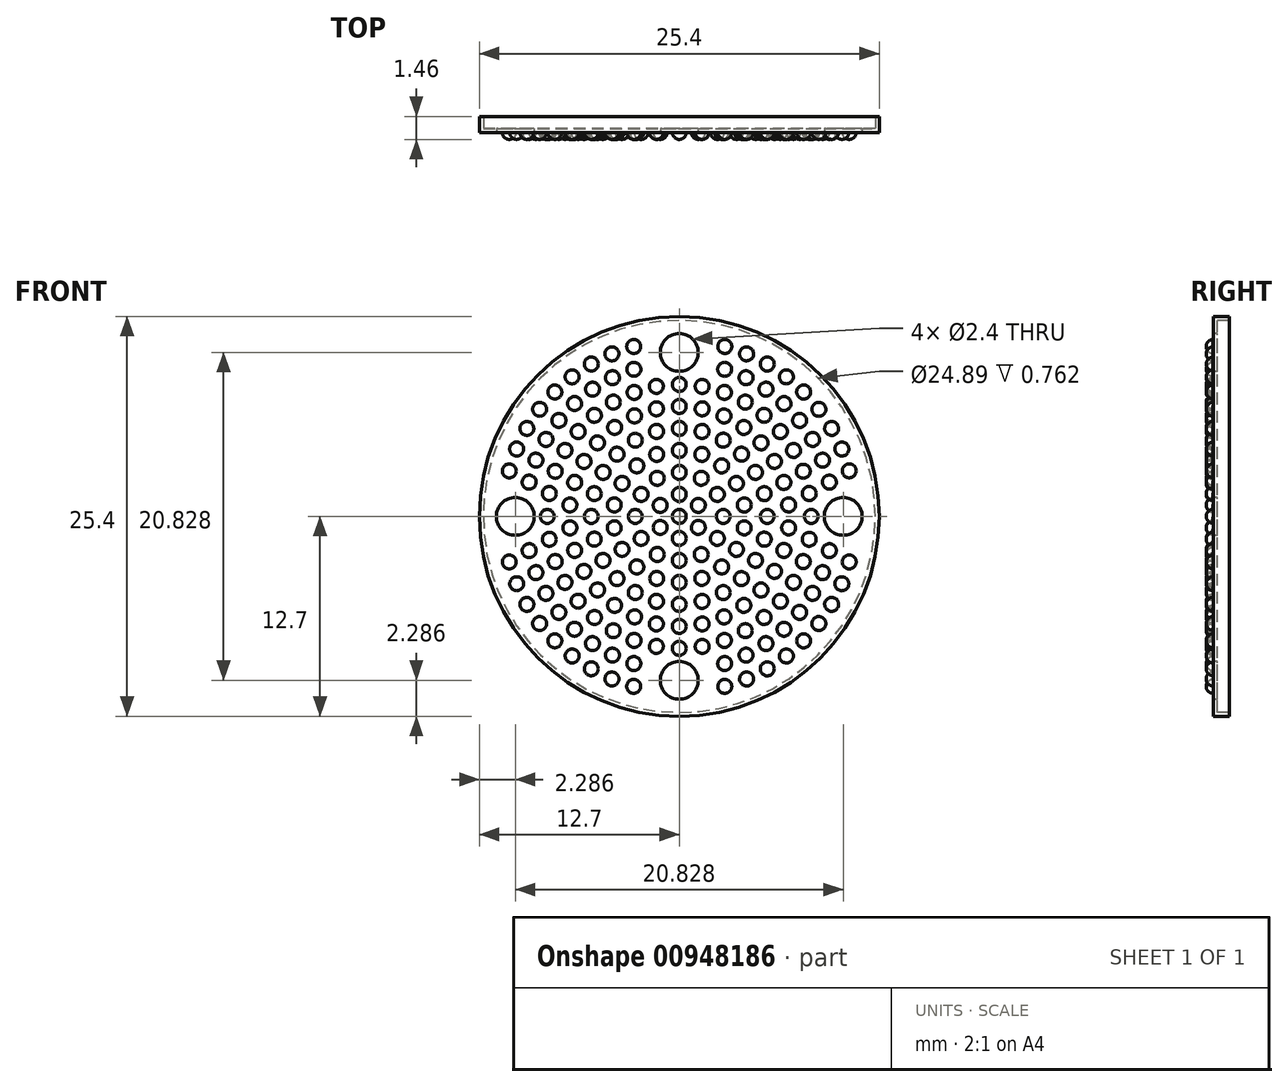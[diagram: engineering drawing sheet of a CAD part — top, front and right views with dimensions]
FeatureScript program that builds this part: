
annotation { "Feature Type Name" : "Feature", "Feature Type Description" : "" }
export const myFeature = defineFeature(function(context is Context, id is Id, definition is map)
    precondition{}
    {
        {
            var Q0;
            Q0=qCreatedBy(makeId("Front.planeOp"),FACE);
            var sketch = newSketch(context, id + "F0", { "sketchPlane" : qUnion([Q0])});
            skCircle(sketch, "E0", {"center": v(0, 0) * mm, "radius": 12.45 * mm});
            skCircle(sketch, "E1.0", {"center": v(0, 0) * mm, "radius": 12.7 * mm});
            skPoint(sketch, "E2", {"position": v(0, 10.41) * mm});
            skPoint(sketch, "E3.3.0", {"position": v(0, 11.18) * mm});
            skPoint(sketch, "E4.1.0", {"position": v(10.41, 0) * mm});
            skPoint(sketch, "E4.2.0", {"position": v(0, -10.41) * mm});
            skPoint(sketch, "E4.3.0", {"position": v(-10.41, 0) * mm});
            skLineSegment(sketch, "E4.anchor1", {"start": v(0, 0) * mm, "end": v(0, 10.41) * mm, "construction": true});
            skLineSegment(sketch, "E4.anchor2", {"start": v(0, 0) * mm, "end": v(-10.41, 0) * mm, "construction": true});
            skSolve(sketch);
        }
        {
            var Q0;
            Q0=makeQuery(id+"F0.imprint","IMPRINT",FACE,{"disambiguationData":[TD([[makeQuery(id+"F0.imprint","IMPRINT",EDGE,{"derivedFrom":sQuery(id+"F0.wireOp",EDGE,"E0")}),1.0]])]});
            extrude(context, id + "F1", {"entities" : qUnion([Q0]), "depth" : -0.25 * mm, "offsetDistance" : 25.4 * mm});
        }
        {
            var Q0;
            Q0=makeQuery(id+"F0.imprint","IMPRINT",FACE,{"disambiguationData":[TD([[makeQuery(id+"F0.imprint","IMPRINT",EDGE,{"derivedFrom":sQuery(id+"F0.wireOp",EDGE,"E0")}),-1.0]])]});
            extrude(context, id + "F2", {"entities" : qUnion([Q0]), "operationType" : NewBodyOperationType.ADD, "depth" : -1.02 * mm, "offsetDistance" : 25.4 * mm});
        }
        {
            var Q0;
            Q0=qCreatedBy(makeId("Right.planeOp"),FACE);
            var sketch = newSketch(context, id + "F3", { "sketchPlane" : qUnion([Q0])});
            skArc(sketch, "E5", {"start": v(0, 0.44) * mm, "mid": v(-0.44, 0) * mm, "end": v(0, -0.44) * mm});
            skLineSegment(sketch, "E6", {"start": v(0, 0.44) * mm, "end": v(0, -0.44) * mm});
            skArc(sketch, "E7.0.1.0", {"start": v(0, 1.84) * mm, "mid": v(-0.44, 1.4) * mm, "end": v(0, 0.95) * mm});
            skLineSegment(sketch, "E7.0.1.1", {"start": v(0, 1.84) * mm, "end": v(0, 0.95) * mm});
            skArc(sketch, "E7.0.2.0", {"start": v(0, 3.24) * mm, "mid": v(-0.44, 2.8) * mm, "end": v(0, 2.35) * mm});
            skLineSegment(sketch, "E7.0.2.1", {"start": v(0, 3.24) * mm, "end": v(0, 2.35) * mm});
            skArc(sketch, "E7.0.3.0", {"start": v(0, 4.64) * mm, "mid": v(-0.44, 4.2) * mm, "end": v(0, 3.75) * mm});
            skLineSegment(sketch, "E7.0.3.1", {"start": v(0, 4.64) * mm, "end": v(0, 3.75) * mm});
            skArc(sketch, "E7.0.4.0", {"start": v(0, 6.03) * mm, "mid": v(-0.44, 5.59) * mm, "end": v(0, 5.14) * mm});
            skLineSegment(sketch, "E7.0.4.1", {"start": v(0, 6.03) * mm, "end": v(0, 5.14) * mm});
            skArc(sketch, "E7.0.5.0", {"start": v(0, 7.43) * mm, "mid": v(-0.44, 6.99) * mm, "end": v(0, 6.54) * mm});
            skLineSegment(sketch, "E7.0.5.1", {"start": v(0, 7.43) * mm, "end": v(0, 6.54) * mm});
            skArc(sketch, "E7.0.6.0", {"start": v(0, 8.83) * mm, "mid": v(-0.44, 8.38) * mm, "end": v(0, 7.94) * mm});
            skLineSegment(sketch, "E7.0.6.1", {"start": v(0, 8.83) * mm, "end": v(0, 7.94) * mm});
            skArc(sketch, "E7.0.7.0", {"start": v(0, 10.22) * mm, "mid": v(-0.44, 9.78) * mm, "end": v(0, 9.33) * mm});
            skLineSegment(sketch, "E7.0.7.1", {"start": v(0, 10.22) * mm, "end": v(0, 9.33) * mm});
            skArc(sketch, "E7.0.8.0", {"start": v(0, 11.62) * mm, "mid": v(-0.44, 11.18) * mm, "end": v(0, 10.73) * mm});
            skLineSegment(sketch, "E7.0.8.1", {"start": v(0, 11.62) * mm, "end": v(0, 10.73) * mm});
            skLineSegment(sketch, "E7.direction1", {"start": v(0, -0.44) * mm, "end": v(25.4, -0.44) * mm, "construction": true});
            skLineSegment(sketch, "E7.direction2", {"start": v(0, -0.44) * mm, "end": v(0, 0.95) * mm, "construction": true});
            skLineSegment(sketch, "E8", {"start": v(0, 0) * mm, "end": v(-1.18, 0) * mm});
            skSolve(sketch);
        }
        {
            var Q0;
            Q0=makeQuery(id+"F3.imprint","IMPRINT",FACE,{"disambiguationData":[TD([[makeQuery(id+"F3.imprint","IMPRINT",EDGE,{"derivedFrom":sQuery(id+"F3.wireOp",EDGE,"E7.0.8.0")}),1.0]])]});
            var Q1;
            Q1=makeQuery(id+"F3.imprint","IMPRINT",FACE,{"disambiguationData":[TD([[makeQuery(id+"F3.imprint","IMPRINT",EDGE,{"derivedFrom":sQuery(id+"F3.wireOp",EDGE,"E7.0.7.0")}),1.0]])]});
            var Q2;
            Q2=makeQuery(id+"F3.imprint","IMPRINT",FACE,{"disambiguationData":[TD([[makeQuery(id+"F3.imprint","IMPRINT",EDGE,{"derivedFrom":sQuery(id+"F3.wireOp",EDGE,"E7.0.6.0")}),1.0]])]});
            var Q3;
            Q3=makeQuery(id+"F3.imprint","IMPRINT",FACE,{"disambiguationData":[TD([[makeQuery(id+"F3.imprint","IMPRINT",EDGE,{"derivedFrom":sQuery(id+"F3.wireOp",EDGE,"E7.0.5.0")}),1.0]])]});
            var Q4;
            Q4=makeQuery(id+"F3.imprint","IMPRINT",FACE,{"disambiguationData":[TD([[makeQuery(id+"F3.imprint","IMPRINT",EDGE,{"derivedFrom":sQuery(id+"F3.wireOp",EDGE,"E7.0.4.0")}),1.0]])]});
            var Q5;
            Q5=makeQuery(id+"F3.imprint","IMPRINT",FACE,{"disambiguationData":[TD([[makeQuery(id+"F3.imprint","IMPRINT",EDGE,{"derivedFrom":sQuery(id+"F3.wireOp",EDGE,"E7.0.3.0")}),1.0]])]});
            var Q6;
            Q6=makeQuery(id+"F3.imprint","IMPRINT",FACE,{"disambiguationData":[TD([[makeQuery(id+"F3.imprint","IMPRINT",EDGE,{"derivedFrom":sQuery(id+"F3.wireOp",EDGE,"E7.0.2.0")}),1.0]])]});
            var Q7;
            Q7=makeQuery(id+"F3.imprint","IMPRINT",FACE,{"disambiguationData":[TD([[makeQuery(id+"F3.imprint","IMPRINT",EDGE,{"derivedFrom":sQuery(id+"F3.wireOp",EDGE,"E7.0.1.0")}),1.0]])]});
            var Q8;
            Q8=sQuery(id+"F3.wireOp",EDGE,"E6");
            revolve(context, id + "F4", {"surfaceOperationType" : NewSurfaceOperationType.NEW, "entities" : qUnion([Q0, Q1, Q2, Q3, Q4, Q5, Q6, Q7]), "axis" : qUnion([Q8]), "revolveType" : RevolveType.TWO_DIRECTIONS, "angle" : 92 * degree, "angleBack" : 272 * degree});
        }
        {
            var Q0;
            {var subQ0=sQuery(id+"F3.wireOp",EDGE,"E6");var subQ1=sQuery(id+"F3.wireOp",EDGE,"E5");var subQ2=makeQuery(id+"F3.imprint","INTERSECT",VERTEX,{"disambiguationData":[OD(1.0)],"derivedFrom":[subQ1,subQ0]});Q0=makeQuery(id+"F3.imprint","IMPRINT",FACE,{"disambiguationData":[TD([[makeQuery(id+"F3.imprint","IMPRINT",EDGE,{"disambiguationData":[TD([[subQ2,1.0]])],"derivedFrom":subQ1}),1.0]])]});}
            var Q1;
            {var subQ0=sQuery(id+"F3.wireOp",EDGE,"E6");var subQ1=sQuery(id+"F3.wireOp",EDGE,"E5");var subQ2=makeQuery(id+"F3.imprint","INTERSECT",VERTEX,{"disambiguationData":[OD(0.0)],"derivedFrom":[subQ1,subQ0]});Q1=makeQuery(id+"F3.imprint","IMPRINT",FACE,{"disambiguationData":[TD([[makeQuery(id+"F3.imprint","IMPRINT",EDGE,{"disambiguationData":[TD([[subQ2,-1.0]])],"derivedFrom":subQ1}),1.0]])]});}
            var Q2;
            Q2=sQuery(id+"F3.wireOp",EDGE,"E6");
            revolve(context, id + "F5", {"operationType" : NewBodyOperationType.ADD, "surfaceOperationType" : NewSurfaceOperationType.NEW, "entities" : qUnion([Q0, Q1]), "axis" : qUnion([Q2]), "revolveType" : RevolveType.TWO_DIRECTIONS, "angle" : 92 * degree, "angleBack" : 272 * degree});
        }
        {
            var Q0;
            Q0=makeQuery(id+"F4.opRevolve","SWEPT_BODY",BODY,{"disambiguationData":[OSD([sQuery(id+"F3.wireOp",EDGE,"E7.0.1.0"),sQuery(id+"F3.wireOp",EDGE,"E7.0.1.1")])]});
            var Q1;
            Q1=sQuery(id+"F3.wireOp",EDGE,"E8");
            circularPattern(context, id + "F6", {"entities" : qUnion([Q0]), "axis" : qUnion([Q1]), "angle" : 360 * degree, "instanceCount" : 6, "equalSpace" : true});
        }
        {
            var Q0;
            Q0=makeQuery(id+"F4.opRevolve","SWEPT_BODY",BODY,{"disambiguationData":[OSD([sQuery(id+"F3.wireOp",EDGE,"E7.0.2.0"),sQuery(id+"F3.wireOp",EDGE,"E7.0.2.1")])]});
            var Q1;
            Q1=sQuery(id+"F3.wireOp",EDGE,"E8");
            circularPattern(context, id + "F7", {"entities" : qUnion([Q0]), "axis" : qUnion([Q1]), "angle" : 360 * degree, "instanceCount" : 12, "equalSpace" : true});
        }
        {
            var Q0;
            Q0=makeQuery(id+"F4.opRevolve","SWEPT_BODY",BODY,{"disambiguationData":[OSD([sQuery(id+"F3.wireOp",EDGE,"E7.0.3.0"),sQuery(id+"F3.wireOp",EDGE,"E7.0.3.1")])]});
            var Q1;
            Q1=sQuery(id+"F3.wireOp",EDGE,"E8");
            circularPattern(context, id + "F8", {"entities" : qUnion([Q0]), "axis" : qUnion([Q1]), "angle" : 360 * degree, "instanceCount" : 18, "equalSpace" : true});
        }
        {
            var Q0;
            Q0=makeQuery(id+"F4.opRevolve","SWEPT_BODY",BODY,{"disambiguationData":[OSD([sQuery(id+"F3.wireOp",EDGE,"E7.0.4.0"),sQuery(id+"F3.wireOp",EDGE,"E7.0.4.1")])]});
            var Q1;
            Q1=sQuery(id+"F3.wireOp",EDGE,"E8");
            circularPattern(context, id + "F9", {"entities" : qUnion([Q0]), "axis" : qUnion([Q1]), "angle" : 360 * degree, "instanceCount" : 24, "equalSpace" : true});
        }
        {
            var Q0;
            Q0=makeQuery(id+"F4.opRevolve","SWEPT_BODY",BODY,{"disambiguationData":[OSD([sQuery(id+"F3.wireOp",EDGE,"E7.0.5.0"),sQuery(id+"F3.wireOp",EDGE,"E7.0.5.1")])]});
            var Q1;
            Q1=sQuery(id+"F3.wireOp",EDGE,"E8");
            circularPattern(context, id + "F10", {"entities" : qUnion([Q0]), "axis" : qUnion([Q1]), "angle" : 360 * degree, "instanceCount" : 30, "equalSpace" : true});
        }
        {
            var Q0;
            Q0=makeQuery(id+"F4.opRevolve","SWEPT_BODY",BODY,{"disambiguationData":[OSD([sQuery(id+"F3.wireOp",EDGE,"E7.0.6.0"),sQuery(id+"F3.wireOp",EDGE,"E7.0.6.1")])]});
            var Q1;
            Q1=sQuery(id+"F3.wireOp",EDGE,"E8");
            circularPattern(context, id + "F11", {"entities" : qUnion([Q0]), "axis" : qUnion([Q1]), "angle" : 360 * degree, "instanceCount" : 36, "equalSpace" : true});
        }
        {
            var Q0;
            Q0=makeQuery(id+"F4.opRevolve","SWEPT_BODY",BODY,{"disambiguationData":[OSD([sQuery(id+"F3.wireOp",EDGE,"E7.0.7.0"),sQuery(id+"F3.wireOp",EDGE,"E7.0.7.1")])]});
            var Q1;
            Q1=sQuery(id+"F3.wireOp",EDGE,"E8");
            circularPattern(context, id + "F12", {"entities" : qUnion([Q0]), "axis" : qUnion([Q1]), "angle" : 360 * degree, "instanceCount" : 42, "equalSpace" : true});
        }
        {
            var Q0;
            Q0=makeQuery(id+"F4.opRevolve","SWEPT_BODY",BODY,{"disambiguationData":[OSD([sQuery(id+"F3.wireOp",EDGE,"E7.0.8.0"),sQuery(id+"F3.wireOp",EDGE,"E7.0.8.1")])]});
            var Q1;
            Q1=sQuery(id+"F3.wireOp",EDGE,"E8");
            circularPattern(context, id + "F13", {"entities" : qUnion([Q0]), "axis" : qUnion([Q1]), "angle" : 360 * degree, "instanceCount" : 48, "equalSpace" : true});
        }
        {
            var Q0;
            Q0=makeQuery(id+"F13.opPattern","COPY",BODY,{"derivedFrom":makeQuery(id+"F4.opRevolve","SWEPT_BODY",BODY,{"disambiguationData":[OSD([sQuery(id+"F3.wireOp",EDGE,"E7.0.8.0"),sQuery(id+"F3.wireOp",EDGE,"E7.0.8.1")])]}),"instanceName":"24"});
            deleteBodies(context, id + "F14", {"entities" : qUnion([Q0])});
        }
        {
            var Q0;
            Q0=makeQuery(id+"F13.opPattern","COPY",BODY,{"derivedFrom":makeQuery(id+"F4.opRevolve","SWEPT_BODY",BODY,{"disambiguationData":[OSD([sQuery(id+"F3.wireOp",EDGE,"E7.0.8.0"),sQuery(id+"F3.wireOp",EDGE,"E7.0.8.1")])]}),"instanceName":"36"});
            var Q1;
            Q1=makeQuery(id+"F4.opRevolve","SWEPT_BODY",BODY,{"disambiguationData":[OSD([sQuery(id+"F3.wireOp",EDGE,"E7.0.8.0"),sQuery(id+"F3.wireOp",EDGE,"E7.0.8.1")])]});
            var Q2;
            Q2=makeQuery(id+"F13.opPattern","COPY",BODY,{"derivedFrom":makeQuery(id+"F4.opRevolve","SWEPT_BODY",BODY,{"disambiguationData":[OSD([sQuery(id+"F3.wireOp",EDGE,"E7.0.8.0"),sQuery(id+"F3.wireOp",EDGE,"E7.0.8.1")])]}),"instanceName":"12"});
            var Q3;
            Q3=makeQuery(id+"F13.opPattern","COPY",BODY,{"derivedFrom":makeQuery(id+"F4.opRevolve","SWEPT_BODY",BODY,{"disambiguationData":[OSD([sQuery(id+"F3.wireOp",EDGE,"E7.0.8.0"),sQuery(id+"F3.wireOp",EDGE,"E7.0.8.1")])]}),"instanceName":"23"});
            var Q4;
            Q4=makeQuery(id+"F12.opPattern","COPY",BODY,{"derivedFrom":makeQuery(id+"F4.opRevolve","SWEPT_BODY",BODY,{"disambiguationData":[OSD([sQuery(id+"F3.wireOp",EDGE,"E7.0.7.0"),sQuery(id+"F3.wireOp",EDGE,"E7.0.7.1")])]}),"instanceName":"20"});
            var Q5;
            Q5=makeQuery(id+"F12.opPattern","COPY",BODY,{"derivedFrom":makeQuery(id+"F4.opRevolve","SWEPT_BODY",BODY,{"disambiguationData":[OSD([sQuery(id+"F3.wireOp",EDGE,"E7.0.7.0"),sQuery(id+"F3.wireOp",EDGE,"E7.0.7.1")])]}),"instanceName":"21"});
            var Q6;
            Q6=makeQuery(id+"F12.opPattern","COPY",BODY,{"derivedFrom":makeQuery(id+"F4.opRevolve","SWEPT_BODY",BODY,{"disambiguationData":[OSD([sQuery(id+"F3.wireOp",EDGE,"E7.0.7.0"),sQuery(id+"F3.wireOp",EDGE,"E7.0.7.1")])]}),"instanceName":"22"});
            var Q7;
            Q7=makeQuery(id+"F13.opPattern","COPY",BODY,{"derivedFrom":makeQuery(id+"F4.opRevolve","SWEPT_BODY",BODY,{"disambiguationData":[OSD([sQuery(id+"F3.wireOp",EDGE,"E7.0.8.0"),sQuery(id+"F3.wireOp",EDGE,"E7.0.8.1")])]}),"instanceName":"25"});
            var Q8;
            Q8=makeQuery(id+"F13.opPattern","COPY",BODY,{"derivedFrom":makeQuery(id+"F4.opRevolve","SWEPT_BODY",BODY,{"disambiguationData":[OSD([sQuery(id+"F3.wireOp",EDGE,"E7.0.8.0"),sQuery(id+"F3.wireOp",EDGE,"E7.0.8.1")])]}),"instanceName":"47"});
            var Q9;
            Q9=makeQuery(id+"F12.opPattern","COPY",BODY,{"derivedFrom":makeQuery(id+"F4.opRevolve","SWEPT_BODY",BODY,{"disambiguationData":[OSD([sQuery(id+"F3.wireOp",EDGE,"E7.0.7.0"),sQuery(id+"F3.wireOp",EDGE,"E7.0.7.1")])]}),"instanceName":"41"});
            var Q10;
            Q10=makeQuery(id+"F4.opRevolve","SWEPT_BODY",BODY,{"disambiguationData":[OSD([sQuery(id+"F3.wireOp",EDGE,"E7.0.7.0"),sQuery(id+"F3.wireOp",EDGE,"E7.0.7.1")])]});
            var Q11;
            Q11=makeQuery(id+"F12.opPattern","COPY",BODY,{"derivedFrom":makeQuery(id+"F4.opRevolve","SWEPT_BODY",BODY,{"disambiguationData":[OSD([sQuery(id+"F3.wireOp",EDGE,"E7.0.7.0"),sQuery(id+"F3.wireOp",EDGE,"E7.0.7.1")])]}),"instanceName":"1"});
            var Q12;
            Q12=makeQuery(id+"F13.opPattern","COPY",BODY,{"derivedFrom":makeQuery(id+"F4.opRevolve","SWEPT_BODY",BODY,{"disambiguationData":[OSD([sQuery(id+"F3.wireOp",EDGE,"E7.0.8.0"),sQuery(id+"F3.wireOp",EDGE,"E7.0.8.1")])]}),"instanceName":"1"});
            var Q13;
            Q13=makeQuery(id+"F13.opPattern","COPY",BODY,{"derivedFrom":makeQuery(id+"F4.opRevolve","SWEPT_BODY",BODY,{"disambiguationData":[OSD([sQuery(id+"F3.wireOp",EDGE,"E7.0.8.0"),sQuery(id+"F3.wireOp",EDGE,"E7.0.8.1")])]}),"instanceName":"11"});
            var Q14;
            Q14=makeQuery(id+"F12.opPattern","COPY",BODY,{"derivedFrom":makeQuery(id+"F4.opRevolve","SWEPT_BODY",BODY,{"disambiguationData":[OSD([sQuery(id+"F3.wireOp",EDGE,"E7.0.7.0"),sQuery(id+"F3.wireOp",EDGE,"E7.0.7.1")])]}),"instanceName":"10"});
            var Q15;
            Q15=makeQuery(id+"F12.opPattern","COPY",BODY,{"derivedFrom":makeQuery(id+"F4.opRevolve","SWEPT_BODY",BODY,{"disambiguationData":[OSD([sQuery(id+"F3.wireOp",EDGE,"E7.0.7.0"),sQuery(id+"F3.wireOp",EDGE,"E7.0.7.1")])]}),"instanceName":"11"});
            var Q16;
            Q16=makeQuery(id+"F13.opPattern","COPY",BODY,{"derivedFrom":makeQuery(id+"F4.opRevolve","SWEPT_BODY",BODY,{"disambiguationData":[OSD([sQuery(id+"F3.wireOp",EDGE,"E7.0.8.0"),sQuery(id+"F3.wireOp",EDGE,"E7.0.8.1")])]}),"instanceName":"13"});
            var Q17;
            Q17=makeQuery(id+"F13.opPattern","COPY",BODY,{"derivedFrom":makeQuery(id+"F4.opRevolve","SWEPT_BODY",BODY,{"disambiguationData":[OSD([sQuery(id+"F3.wireOp",EDGE,"E7.0.8.0"),sQuery(id+"F3.wireOp",EDGE,"E7.0.8.1")])]}),"instanceName":"35"});
            var Q18;
            Q18=makeQuery(id+"F12.opPattern","COPY",BODY,{"derivedFrom":makeQuery(id+"F4.opRevolve","SWEPT_BODY",BODY,{"disambiguationData":[OSD([sQuery(id+"F3.wireOp",EDGE,"E7.0.7.0"),sQuery(id+"F3.wireOp",EDGE,"E7.0.7.1")])]}),"instanceName":"31"});
            var Q19;
            Q19=makeQuery(id+"F12.opPattern","COPY",BODY,{"derivedFrom":makeQuery(id+"F4.opRevolve","SWEPT_BODY",BODY,{"disambiguationData":[OSD([sQuery(id+"F3.wireOp",EDGE,"E7.0.7.0"),sQuery(id+"F3.wireOp",EDGE,"E7.0.7.1")])]}),"instanceName":"32"});
            var Q20;
            Q20=makeQuery(id+"F13.opPattern","COPY",BODY,{"derivedFrom":makeQuery(id+"F4.opRevolve","SWEPT_BODY",BODY,{"disambiguationData":[OSD([sQuery(id+"F3.wireOp",EDGE,"E7.0.8.0"),sQuery(id+"F3.wireOp",EDGE,"E7.0.8.1")])]}),"instanceName":"37"});
            deleteBodies(context, id + "F15", {"entities" : qUnion([Q0, Q1, Q2, Q3, Q4, Q5, Q6, Q7, Q8, Q9, Q10, Q11, Q12, Q13, Q14, Q15, Q16, Q17, Q18, Q19, Q20])});
        }
        {
            var Q0;
            Q0=sQuery(id+"F0.wireOp",VERTEX,"E2");
            var Q1;
            Q1=sQuery(id+"F0.wireOp",VERTEX,"E4.1.0");
            var Q2;
            Q2=sQuery(id+"F0.wireOp",VERTEX,"E4.2.0");
            var Q3;
            Q3=sQuery(id+"F0.wireOp",VERTEX,"E4.3.0");
            var Q4;
            Q4=makeQuery(id+"F1.opExtrude","SWEPT_BODY",BODY,{"disambiguationData":[OSD([sQuery(id+"F0.wireOp",EDGE,"E0")])]});
            hole(context, id + "F16", {"style" : HoleStyle.C_SINK, "endStyle" : HoleEndStyle.THROUGH, "standardTappedOrClearance" : lookupTablePath({ "fit" : "Normal", "standard" : "ISO", "size" : "M2", "type" : "Clearance" }), "standardBlindInLast" : lookupTablePath({ "fit" : "Normal", "standard" : "ISO", "engagement" : "75%", "pitch" : "0.25 mm", "size" : "M2", "type" : "Clearance & tapped" }), "holeDiameter" : 2.4 * mm, "cSinkDiameter" : 2.4 * mm, "cSinkAngle" : 90 * degree, "majorDiameter" : 6.35 * mm, "isTappedThrough" : true, "tappedDepth" : 12.7 * mm, "tapClearance" : 3, "locations" : qUnion([Q0, Q1, Q2, Q3]), "scope" : qUnion([Q4])});
        }
    });
